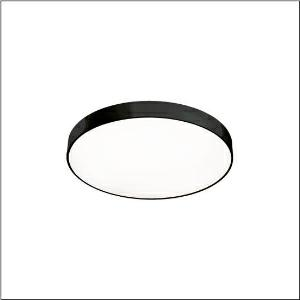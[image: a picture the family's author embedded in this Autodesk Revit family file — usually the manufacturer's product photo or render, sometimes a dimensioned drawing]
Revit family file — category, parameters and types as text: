
# Revit family: round_21_m_51mr36fm8321b
name_source: partatom
category: Lighting Fixtures
units: mm (PartAtom-declared; Revit-internal decimal feet)

## family parameters
Cut with Voids When Loaded = No
Host = Face
Light Source = No
Part Type = Normal
Room Calculation Point = No
Round Connector Dimension = Use Diameter
Shared = No

## types (1)
- --- (1 x LED, 7770 lm, 61.1 W, 3000K)
    Apparent Load = 61 VA
    CIE Flux Codes = 49 80 96 100 100
    Color Rendering = 80
    Color Temperature = 3000K
    Default Elevation = 1800 mm
    Description = Round 21 M, wall and ceiling luminaire, primary optical cover: cover, of PMMA, opal, light emission: direct distribution, primary light characteristic: symmetric, installation type: surface-mounted, suspended mounting, LED, rated luminous flux: 7.700lm, luminous efficacy: 127lm/W, light colour: 830, colour temperature: 3000K, with terminal, 3-pole, mains connection: 230V, AC, 50/60Hz, rated input power: 61W, housing, of aluminium, coated, black, diameter: 600mm, height: 62mm, protection rating (complete): IP40, insulation class (complete): insulation class I (protective earthing), certification: CE, impact resistance: IK04, permissible operating ambient temperature: -10..+35°C, packaging unit: 1 piece
    Height = 87 mm
    Lamp = 1 x LED
    Lamp Light Flux = 7770 lm
    Lamp Power = 61.1 W
    Lamp count = 1
    Length = 600 mm
    Luminous efficacy = 127 lm/W
    Manufacturer = Siteco
    ModVariant = No
    Model = 51MR36FM8321B
    Mounting Place = Ceiling
    Mounting Type = Surface mounted
    Number of Poles = 1
    OnlyDefault = Yes
    Power Factor = 1
    Product Name = Round 21 M
    Product group = wall and ceiling luminaire
    ProductGroupID = 301
    Protection Class = Protection class I
    Protection Degree = IP 40
    RLX_Detail_Level = 1
    RLX_Emergency_Light_Flux = 0 lm
    RLX_Emergency_Type = 0
    RLX_Emergency_Type_DB = No
    RlxData = <blob elided: 20361 chars, md5=971e660c>
    Socket = socket
    Standby Power = 0 W
    System Light Flux = 7770 lm
    System Power = 61 W
    Type Comments = factory setting: luminous flux: 100 % | (ON | ON | ON | ON) | 700 mA
    Type Image = l_1258332.jpg
    URL = http://relux.com
    VarID = @adj_009745
    Voltage = 0 V
    Weight = 0.00 kg
    Width = 0 mm  [stored 0 ft]

note: [stored X ft] marks values corroborated as IEEE doubles in the binary element streams (Revit-internal decimal feet)

## geometry (parser evidence)
native form markers: Blend x4, Sweep x11
no freeform markers — native parametric forms only
